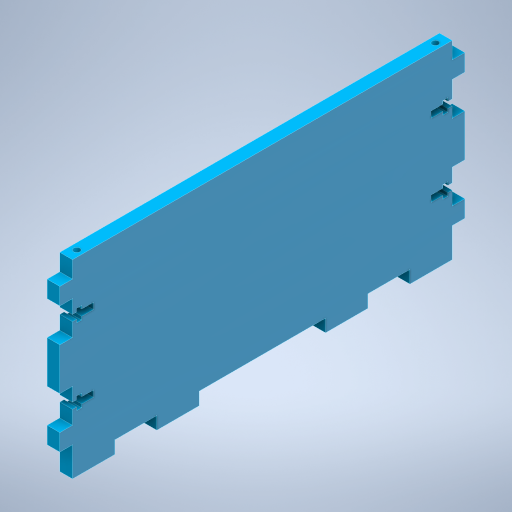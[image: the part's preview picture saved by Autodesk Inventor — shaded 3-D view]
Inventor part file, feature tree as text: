
AUTODESK INVENTOR PART (.ipt)
format: ipt  version: 2024.2 (Build 282272000, 272)  size: 390,656 bytes
history: native  units: mm
features: extrude x4, sketch x4, other x1
ambient origin geometry x8: Origin, YZ Plane, XZ Plane, XY Plane, X Axis, Y Axis, Z Axis, Center Point
bodies: Body1 (feature_tree)
feature tree (9):
  other  "Твердое тело1"
  extrude  "Выдавливание1"  Depth=180.0mm
  extrude  "Выдавливание4"  Depth=84.0mm
  extrude  "Выдавливание5"  Depth=90.0mm
  extrude  "Выдавливание7"  TaperAngle=0.0deg  [1 undecoded]
  sketch  "Эскиз1"
  sketch  "Эскиз4"
  sketch  "Эскиз6"
  sketch  "Эскиз8"
note: 1 required parameter value undecoded (feature->parameter linkage not recoverable at this tier; creation-order binding heuristic only, values carry confidence <= 0.55)
